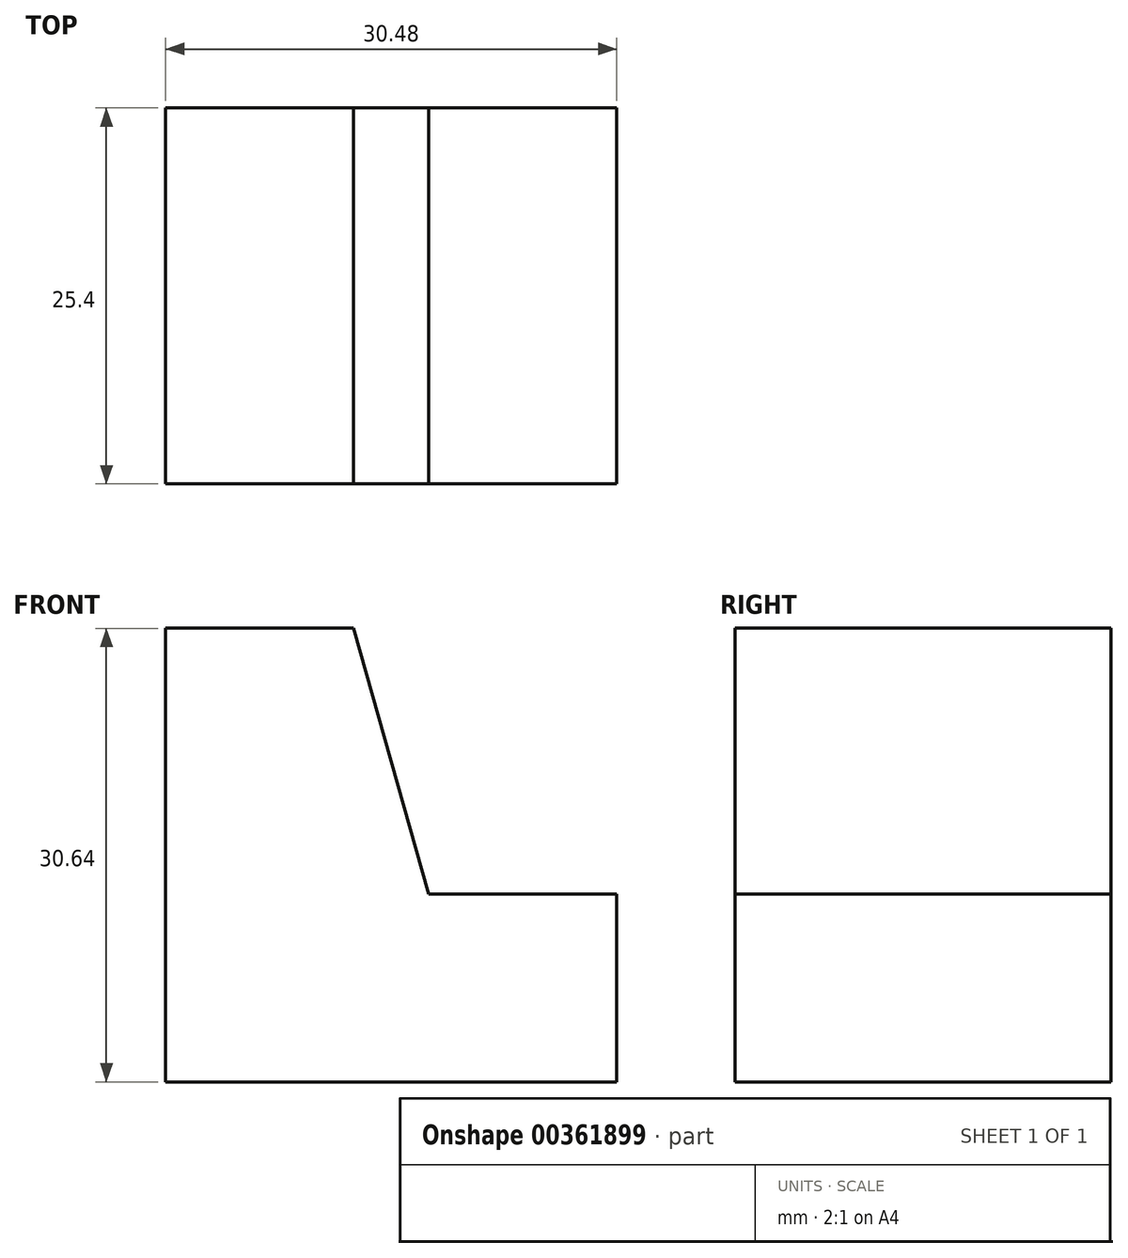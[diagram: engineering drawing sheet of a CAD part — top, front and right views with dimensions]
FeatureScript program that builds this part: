
annotation { "Feature Type Name" : "Feature", "Feature Type Description" : "" }
export const myFeature = defineFeature(function(context is Context, id is Id, definition is map)
    precondition{}
    {
        {
            var Q0;
            Q0=qCreatedBy(makeId("Front.planeOp"),FACE);
            var sketch = newSketch(context, id + "F0", { "sketchPlane" : qUnion([Q0])});
            skLineSegment(sketch, "E0", {"start": v(0, -1.1) * mm, "end": v(0, 30.64) * mm});
            skLineSegment(sketch, "E1", {"start": v(0, 30.64) * mm, "end": v(12.7, 30.64) * mm});
            skLineSegment(sketch, "E2", {"start": v(12.7, 30.64) * mm, "end": v(17.78, 12.7) * mm});
            skLineSegment(sketch, "E3", {"start": v(17.78, 12.7) * mm, "end": v(30.48, 12.7) * mm});
            skLineSegment(sketch, "E4", {"start": v(30.48, 12.7) * mm, "end": v(30.48, 0) * mm});
            skLineSegment(sketch, "E5", {"start": v(30.48, 0) * mm, "end": v(0, 0) * mm});
            skSolve(sketch);
        }
        {
            var Q0;
            Q0 = qSketchRegion(id + "F0", true);
            extrude(context, id + "F1", {"entities" : qUnion([Q0]), "depth" : 25.4 * mm});
        }
    });
